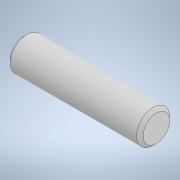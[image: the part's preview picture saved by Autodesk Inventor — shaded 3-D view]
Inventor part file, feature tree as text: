
AUTODESK INVENTOR PART (.ipt)
format: ipt  version: 2022 (Build 260153000, 153)  size: 112,128 bytes
history: native  units: in
note: dims shown in document units (in); Inventor stores cm internally (conversion verified against a paired STEP export)
features: chamfer x1
ambient origin geometry x8: Origin, YZ Plane, XZ Plane, XY Plane, X Axis, Y Axis, Z Axis, Center Point
bodies: Solid1 (feature_tree)
feature tree (1):
  chamfer  "Chamfer1"  [1 undecoded]
note: 1 required parameter value undecoded (feature->parameter linkage not recoverable at this tier; creation-order binding heuristic only, values carry confidence <= 0.55)
